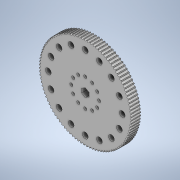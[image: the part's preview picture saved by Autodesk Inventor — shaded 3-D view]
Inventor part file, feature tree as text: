
AUTODESK INVENTOR PART (.ipt)
format: ipt  version: 2020 (Build 240168000, 168)  size: 593,920 bytes
history: native  units: in
note: dims shown in document units (in); Inventor stores cm internally (conversion verified against a paired STEP export)
features: extrude x4, sketch x4, pattern_circular x1
ambient origin geometry x8: Origin, YZ Plane, XZ Plane, XY Plane, X Axis, Y Axis, Z Axis, Center Point
bodies: Solid1 (feature_tree)
feature tree (9):
  extrude  "Extrusion1"  Depth=0.6299in TaperAngle=0.0deg
  extrude  "Extrusion2"  TaperAngle=0.0deg  [1 undecoded]
  pattern_circular  "Circular Pattern1"  Count=100 Angle=360.0deg
  extrude  "Extrusion7"  Depth=0.3848in
  extrude  "Extrusion8"  Depth=0.5in TaperAngle=360.0deg
  sketch  "Sketch1"  dims[d0=6.2209in d1=0.6299in d2=0.0in]
  sketch  "Sketch2"  dims[d3=0.0607in d5=0.0in d6=0.0in d7=39.3701in d8=360.0deg]
  sketch  "Sketch7"  dims[d47=0.082in d50=0.3848in]
  sketch  "Sketch8"  dims[d51=2.497in d52=6.2992in d54=360.0deg d56=0.0in d57=0.0in d58=0.203in d59=0.9375in d60=4.7244in d62=360.0deg d64=0.5in d65=0.0in d66=0.0in]
note: 1 required parameter value undecoded (feature->parameter linkage not recoverable at this tier; creation-order binding heuristic only, values carry confidence <= 0.55)
